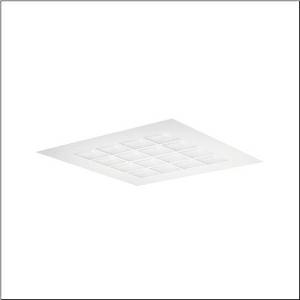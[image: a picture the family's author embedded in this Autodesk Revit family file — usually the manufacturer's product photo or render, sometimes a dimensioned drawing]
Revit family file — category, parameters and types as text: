
# Revit family: scriptus_r__11_5mz312ledzm00191xx_ec59
name_source: partatom
category: Lighting Fixtures
units: mm (PartAtom-declared; Revit-internal decimal feet)

## family parameters
Cut with Voids When Loaded = No
Host = Face
Light Source = No
Part Type = Normal
Room Calculation Point = No
Round Connector Dimension = Use Diameter
Shared = No

## types (1)
- Scriptus® 11 (1 x LED, 6400 lm, 37.5 W, 4000K)
    Apparent Load = 38 VA
    CIE Flux Codes = 80 95 99 100 100
    Color Rendering = 80
    Color Temperature = 4000K
    Default Elevation = 1800 mm
    Description = Scriptus® 11, office luminaire, primary optical cover: lenses, CAT 2 (L<= 3000cd/m²), light emission: direct distribution, primary light characteristic: symmetric, installation type: lay-in mounting, LED, rated luminous flux: 6.400lm, light colour: 840, colour temperature: 4000K, control gear: DALI, with terminal, 3+2-pole, max. 2.5mm², mains connection: 230V, AC, 50Hz, housing, of sheet steel, galvanised, traffic white (RAL 9016), module: M625, length: 621mm, width: 621mm, height: 68mm, protection rating (complete): IP20, insulation class (complete): insulation class I (protective earthing), certification: CE, impact resistance: IK02, permissible operating ambient temperature: 0..+35°C, standard: EN 50419, packaging unit: 1 piece
    Height = 80 mm  [stored 0.262467 ft]
    Lamp = 1 x LED
    Lamp Light Flux = 6400 lm
    Lamp Power = 37.5 W
    Lamp count = 1
    Length = 622 mm
    Luminous efficacy = 171 lm/W
    Manufacturer = Siteco
    ModVariant = No
    Model = 5MZ312LEDZM00191XX
    Mounting Place = Ceiling
    Mounting Type = Pendant
    Number of Poles = 1
    OnlyDefault = Yes
    Power Factor = 1
    Product Name = Scriptus® 11
    Product group = office luminaire | ceiling pendant
    ProductGroupID = 903
    Protection Class = Protection class I
    Protection Degree = IP 20
    RLX_Detail_Level = 1
    RLX_Emergency_Light_Flux = 0 lm
    RLX_Emergency_Type = 0
    RLX_Emergency_Type_DB = No
    RlxData = <blob elided: 19009 chars, md5=4240b4ff>
    Socket = socket
    Standby Power = 0 W
    System Light Flux = 6400 lm
    System Power = 38 W
    Type Comments = Product without accessories
    Type Image = l_1006857.jpg
    URL = http://relux.com
    VarID = ---
    Voltage = 0 V
    Weight = 0.00 kg
    Width = 622 mm

note: [stored X ft] marks values corroborated as IEEE doubles in the binary element streams (Revit-internal decimal feet)

## geometry (parser evidence)
native form markers: Blend x4, Sweep x9
no freeform markers — native parametric forms only
